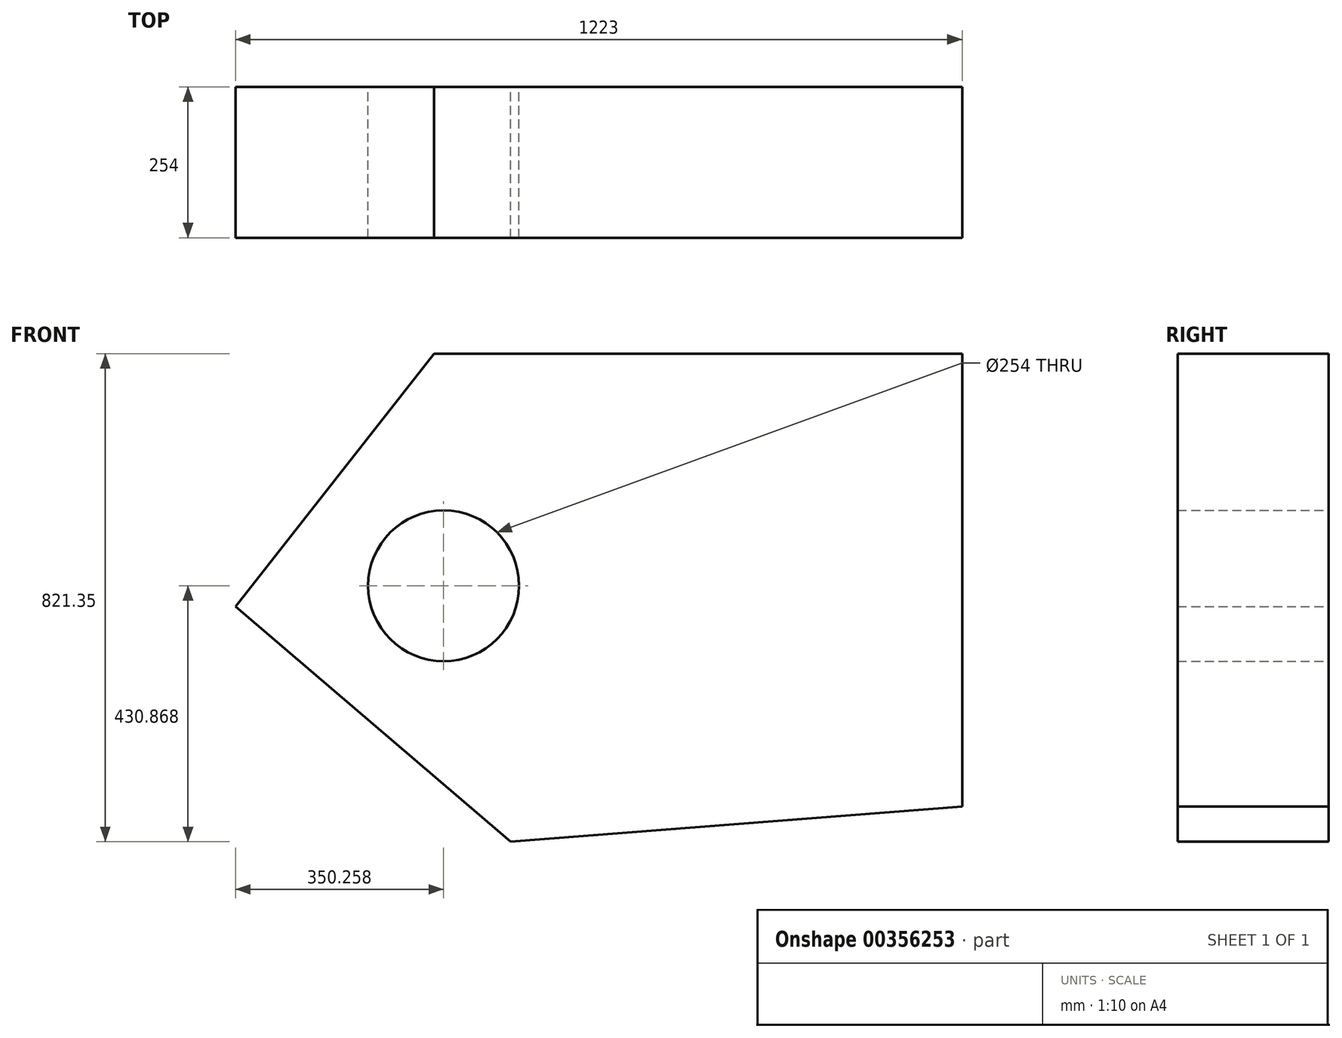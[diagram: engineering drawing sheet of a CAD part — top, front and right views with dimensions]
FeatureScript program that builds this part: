
annotation { "Feature Type Name" : "Feature", "Feature Type Description" : "" }
export const myFeature = defineFeature(function(context is Context, id is Id, definition is map)
    precondition{}
    {
        {
            var Q0;
            Q0=qCreatedBy(makeId("Front.planeOp"),FACE);
            var sketch = newSketch(context, id + "F0", { "sketchPlane" : qUnion([Q0])});
            skLineSegment(sketch, "E0", {"start": v(-411.83, 481.62) * mm, "end": v(-745.83, 56.44) * mm});
            skLineSegment(sketch, "E1", {"start": v(-745.83, 56.44) * mm, "end": v(-282.51, -339.73) * mm});
            skLineSegment(sketch, "E2", {"start": v(-411.83, 481.62) * mm, "end": v(477.17, 481.62) * mm});
            skLineSegment(sketch, "E3", {"start": v(477.17, 481.62) * mm, "end": v(477.17, -280.38) * mm});
            skLineSegment(sketch, "E4", {"start": v(477.17, -280.38) * mm, "end": v(-282.51, -339.73) * mm});
            skCircle(sketch, "E5", {"center": v(-395.57, 91.14) * mm, "radius": 127 * mm});
            skSolve(sketch);
        }
        {
            var Q0;
            Q0=makeQuery(id+"F0.imprint","IMPRINT",FACE,{"disambiguationData":[TD([[makeQuery(id+"F0.imprint","IMPRINT",EDGE,{"derivedFrom":sQuery(id+"F0.wireOp",EDGE,"E0")}),1.0]])]});
            extrude(context, id + "F1", {"entities" : qUnion([Q0]), "depth" : 254 * mm});
        }
    });
